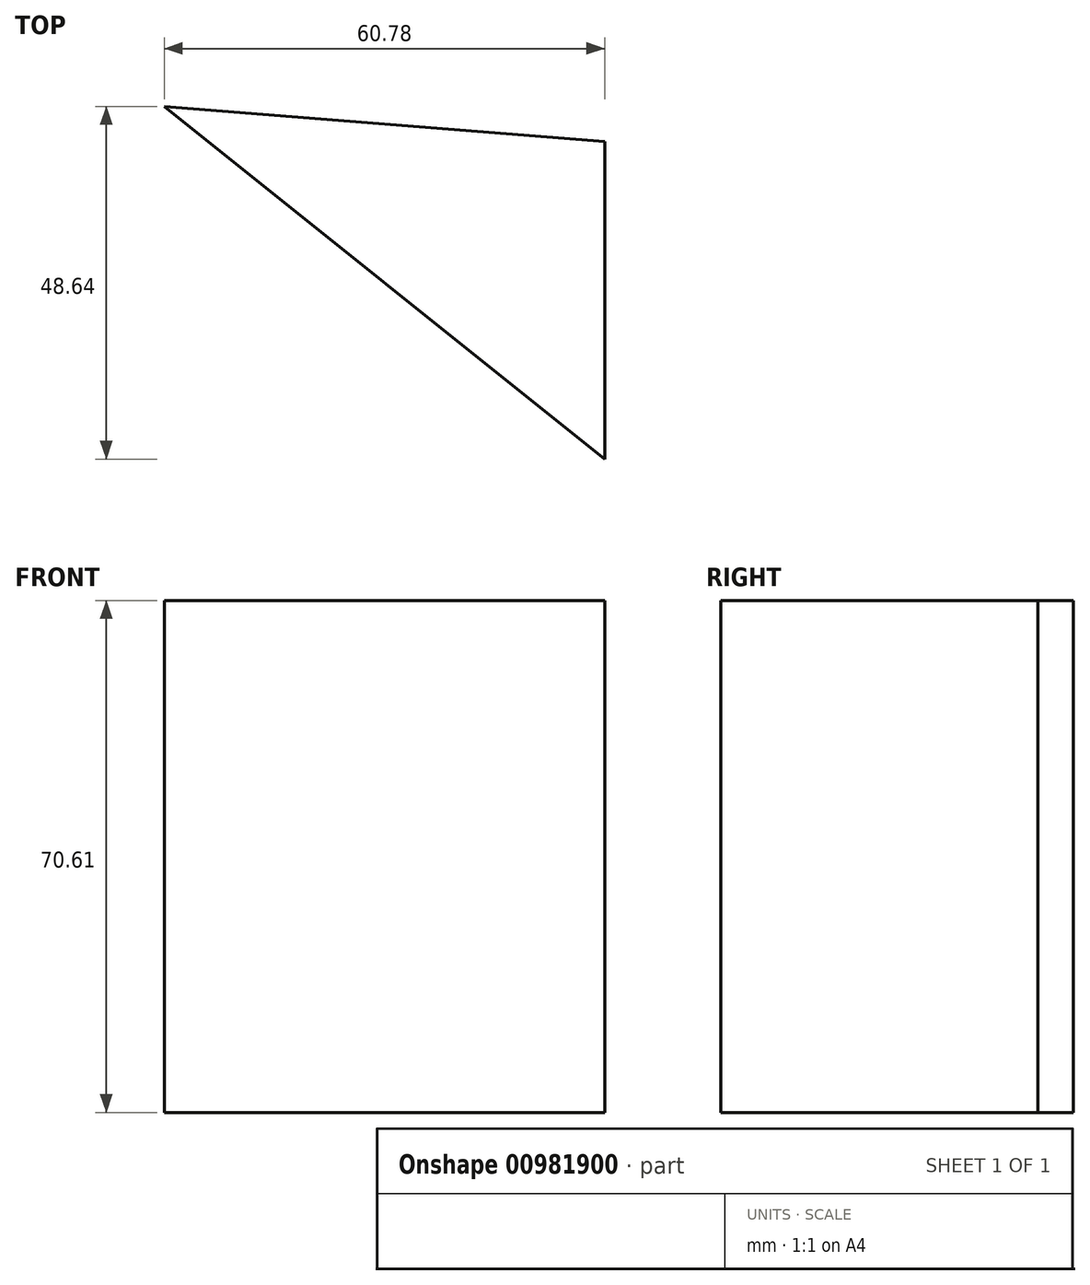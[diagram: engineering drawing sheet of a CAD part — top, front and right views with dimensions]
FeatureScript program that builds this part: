
annotation { "Feature Type Name" : "Feature", "Feature Type Description" : "" }
export const myFeature = defineFeature(function(context is Context, id is Id, definition is map)
    precondition{}
    {
        {
            var Q0;
            Q0=qCreatedBy(makeId("Top.planeOp"),FACE);
            var sketch = newSketch(context, id + "F0", { "sketchPlane" : qUnion([Q0])});
            skLineSegment(sketch, "E0", {"start": v(-35.47, 25.01) * mm, "end": v(25.31, -23.63) * mm});
            skLineSegment(sketch, "E1", {"start": v(25.31, -23.63) * mm, "end": v(25.31, 20.15) * mm});
            skLineSegment(sketch, "E2", {"start": v(25.31, 20.15) * mm, "end": v(-35.47, 25.01) * mm});
            skSolve(sketch);
        }
        {
            var Q0;
            Q0 = qSketchRegion(id + "F0", true);
            extrude(context, id + "F1", {"entities" : qUnion([Q0]), "depth" : 70.6 * mm, "offsetDistance" : 25.4 * mm});
        }
    });
